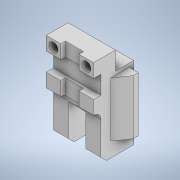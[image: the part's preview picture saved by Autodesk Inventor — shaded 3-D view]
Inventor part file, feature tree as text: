
AUTODESK INVENTOR PART (.ipt)
format: ipt  version: 2022 (Build 260153000, 153)  size: 219,648 bytes
history: native  units: mm
features: extrude x7, sketch x4, other x1, chamfer x1, fillet x1
ambient origin geometry x8: Origin, YZ Plane, XZ Plane, XY Plane, X Axis, Y Axis, Z Axis, Center Point
bodies: Body1 (feature_tree)
feature tree (14):
  other  "Sólido1"
  sketch  "Esboço1"  dims[d0=19.0mm d1=52.0mm]
  extrude  "Extrusão1"  Depth=52.0mm
  extrude  "Extrusão2"  Depth=100.0mm
  extrude  "Extrusão3"  Depth=20.0mm
  extrude  "Extrusão4"  Depth=10.0mm
  chamfer  "Chanfro1"  Distance=10.0mm
  fillet  "Arredondamento1"  Radius=36.0mm
  extrude  "Extrusão5"  Depth=20.0mm
  extrude  "Extrusão6"  Depth=16.0mm
  extrude  "Extrusão7"  Depth=16.0mm
  sketch  "Esboço2"  dims[d2=41.0mm d3=100.0mm]
  sketch  "Esboço3"  dims[d4=15.0mm d5=20.0mm]
  sketch  "Esboço4"  dims[d6=50.0mm d7=10.0mm d8=10.0mm d9=36.0mm d10=20.0mm d12=16.0mm d13=16.0mm d14=8.0mm d15=8.0mm d16=7.5mm d17=7.5mm d18=20.0mm d19=24.0mm d20=0.0mm d21=16.0mm d22=0.0mm d23=19.0mm d24=0.0mm d25=20.0mm d26=0.0mm d27=6.0mm d28=2.0mm d29=45.0deg d30=8.0mm d31=60.0mm d32=20.0mm d34=16.0mm d35=5.0mm d36=10.0mm d37=0.0mm d38=60.0mm d39=20.0mm d40=16.0mm d41=5.0mm d42=10.0mm d43=0.0mm d46=6.108652mm d47=6.108652mm d48=0.0mm d49=0.0mm]
